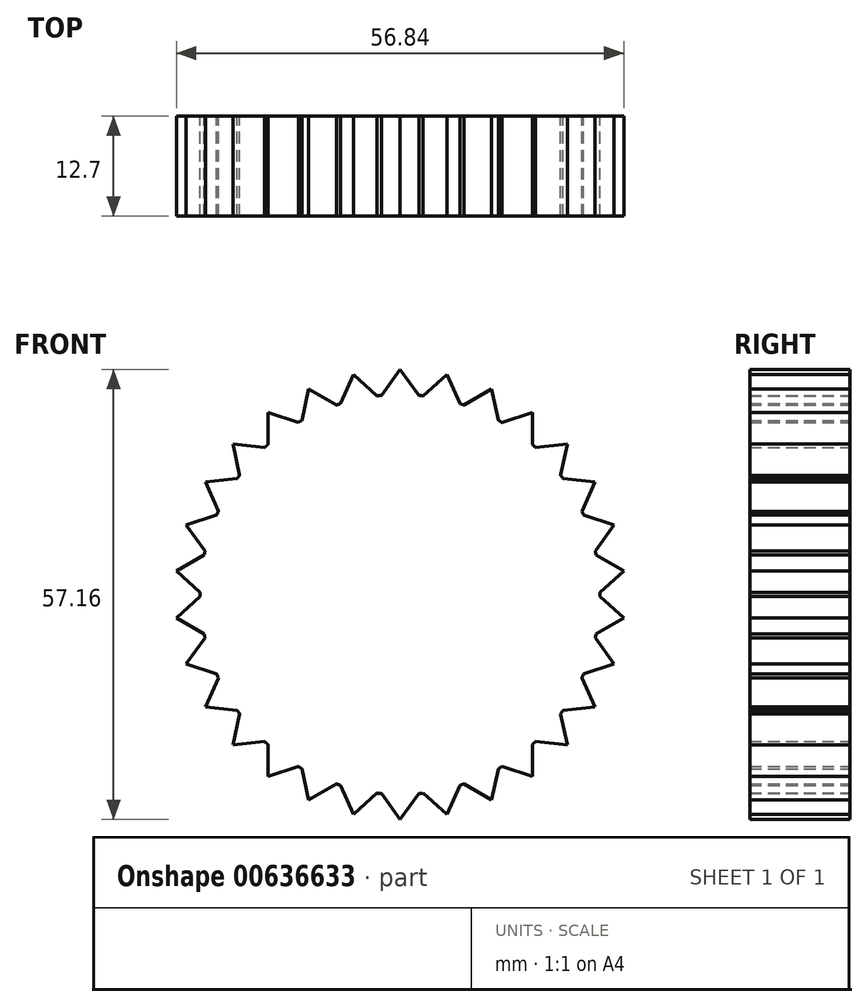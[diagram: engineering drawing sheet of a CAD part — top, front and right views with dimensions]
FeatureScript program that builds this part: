
annotation { "Feature Type Name" : "Feature", "Feature Type Description" : "" }
export const myFeature = defineFeature(function(context is Context, id is Id, definition is map)
    precondition{}
    {
        {
            var Q0;
            Q0=qCreatedBy(makeId("Front.planeOp"),FACE);
            var sketch = newSketch(context, id + "F0", { "sketchPlane" : qUnion([Q0])});
            skCircle(sketch, "E0", {"center": v(0, 0) * mm, "radius": 25.4 * mm});
            skLineSegment(sketch, "E1", {"start": v(0, 25.4) * mm, "end": v(0, 28.58) * mm});
            skLineSegment(sketch, "E2", {"start": v(0, 28.58) * mm, "end": v(-2.39, 25.29) * mm});
            skLineSegment(sketch, "E3.MirrorCS", {"start": v(0, 28.58) * mm, "end": v(2.39, 25.29) * mm});
            skLineSegment(sketch, "E4.1.0", {"start": v(-5.94, 27.95) * mm, "end": v(-7.6, 24.24) * mm});
            skLineSegment(sketch, "E4.1.1", {"start": v(-5.94, 27.95) * mm, "end": v(-2.92, 25.23) * mm});
            skLineSegment(sketch, "E4.2.0", {"start": v(-11.62, 26.1) * mm, "end": v(-12.47, 22.13) * mm});
            skLineSegment(sketch, "E4.2.1", {"start": v(-11.62, 26.1) * mm, "end": v(-8.1, 24.07) * mm});
            skLineSegment(sketch, "E4.3.0", {"start": v(-16.8, 23.12) * mm, "end": v(-16.8, 19.05) * mm});
            skLineSegment(sketch, "E4.3.1", {"start": v(-16.8, 23.12) * mm, "end": v(-12.93, 21.86) * mm});
            skLineSegment(sketch, "E4.4.0", {"start": v(-21.24, 19.12) * mm, "end": v(-20.4, 15.15) * mm});
            skLineSegment(sketch, "E4.4.1", {"start": v(-21.24, 19.12) * mm, "end": v(-17.2, 18.7) * mm});
            skLineSegment(sketch, "E4.5.0", {"start": v(-24.75, 14.29) * mm, "end": v(-23.1, 10.58) * mm});
            skLineSegment(sketch, "E4.5.1", {"start": v(-24.75, 14.29) * mm, "end": v(-20.7, 14.71) * mm});
            skLineSegment(sketch, "E4.6.0", {"start": v(-27.18, 8.83) * mm, "end": v(-24.79, 5.54) * mm});
            skLineSegment(sketch, "E4.6.1", {"start": v(-27.18, 8.83) * mm, "end": v(-23.31, 10.09) * mm});
            skLineSegment(sketch, "E4.7.0", {"start": v(-28.42, 2.99) * mm, "end": v(-25.4, 0.27) * mm});
            skLineSegment(sketch, "E4.7.1", {"start": v(-28.42, 2.99) * mm, "end": v(-24.9, 5.02) * mm});
            skLineSegment(sketch, "E4.8.0", {"start": v(-28.42, -2.99) * mm, "end": v(-24.9, -5.02) * mm});
            skLineSegment(sketch, "E4.8.1", {"start": v(-28.42, -2.99) * mm, "end": v(-25.4, -0.27) * mm});
            skLineSegment(sketch, "E4.9.0", {"start": v(-27.18, -8.83) * mm, "end": v(-23.31, -10.09) * mm});
            skLineSegment(sketch, "E4.9.1", {"start": v(-27.18, -8.83) * mm, "end": v(-24.79, -5.54) * mm});
            skLineSegment(sketch, "E4.10.0", {"start": v(-24.75, -14.29) * mm, "end": v(-20.7, -14.71) * mm});
            skLineSegment(sketch, "E4.10.1", {"start": v(-24.75, -14.29) * mm, "end": v(-23.1, -10.58) * mm});
            skLineSegment(sketch, "E4.11.0", {"start": v(-21.24, -19.12) * mm, "end": v(-17.2, -18.7) * mm});
            skLineSegment(sketch, "E4.11.1", {"start": v(-21.24, -19.12) * mm, "end": v(-20.4, -15.15) * mm});
            skLineSegment(sketch, "E4.12.0", {"start": v(-16.8, -23.12) * mm, "end": v(-12.93, -21.86) * mm});
            skLineSegment(sketch, "E4.12.1", {"start": v(-16.8, -23.12) * mm, "end": v(-16.8, -19.05) * mm});
            skLineSegment(sketch, "E4.13.0", {"start": v(-11.62, -26.1) * mm, "end": v(-8.1, -24.07) * mm});
            skLineSegment(sketch, "E4.13.1", {"start": v(-11.62, -26.1) * mm, "end": v(-12.47, -22.13) * mm});
            skLineSegment(sketch, "E4.14.0", {"start": v(-5.94, -27.95) * mm, "end": v(-2.92, -25.23) * mm});
            skLineSegment(sketch, "E4.14.1", {"start": v(-5.94, -27.95) * mm, "end": v(-7.6, -24.24) * mm});
            skLineSegment(sketch, "E4.15.0", {"start": v(0, -28.58) * mm, "end": v(2.39, -25.29) * mm});
            skLineSegment(sketch, "E4.15.1", {"start": v(0, -28.58) * mm, "end": v(-2.39, -25.29) * mm});
            skLineSegment(sketch, "E4.16.0", {"start": v(5.94, -27.95) * mm, "end": v(7.6, -24.24) * mm});
            skLineSegment(sketch, "E4.16.1", {"start": v(5.94, -27.95) * mm, "end": v(2.92, -25.23) * mm});
            skLineSegment(sketch, "E4.17.0", {"start": v(11.62, -26.1) * mm, "end": v(12.47, -22.13) * mm});
            skLineSegment(sketch, "E4.17.1", {"start": v(11.62, -26.1) * mm, "end": v(8.1, -24.07) * mm});
            skLineSegment(sketch, "E4.18.0", {"start": v(16.8, -23.12) * mm, "end": v(16.8, -19.05) * mm});
            skLineSegment(sketch, "E4.18.1", {"start": v(16.8, -23.12) * mm, "end": v(12.93, -21.86) * mm});
            skLineSegment(sketch, "E4.19.0", {"start": v(21.24, -19.12) * mm, "end": v(20.4, -15.15) * mm});
            skLineSegment(sketch, "E4.19.1", {"start": v(21.24, -19.12) * mm, "end": v(17.2, -18.7) * mm});
            skLineSegment(sketch, "E4.20.0", {"start": v(24.75, -14.29) * mm, "end": v(23.1, -10.58) * mm});
            skLineSegment(sketch, "E4.20.1", {"start": v(24.75, -14.29) * mm, "end": v(20.7, -14.71) * mm});
            skLineSegment(sketch, "E4.21.0", {"start": v(27.18, -8.83) * mm, "end": v(24.79, -5.54) * mm});
            skLineSegment(sketch, "E4.21.1", {"start": v(27.18, -8.83) * mm, "end": v(23.31, -10.09) * mm});
            skLineSegment(sketch, "E4.22.0", {"start": v(28.42, -2.99) * mm, "end": v(25.4, -0.27) * mm});
            skLineSegment(sketch, "E4.22.1", {"start": v(28.42, -2.99) * mm, "end": v(24.9, -5.02) * mm});
            skLineSegment(sketch, "E4.23.0", {"start": v(28.42, 2.99) * mm, "end": v(24.9, 5.02) * mm});
            skLineSegment(sketch, "E4.23.1", {"start": v(28.42, 2.99) * mm, "end": v(25.4, 0.27) * mm});
            skLineSegment(sketch, "E4.24.0", {"start": v(27.18, 8.83) * mm, "end": v(23.31, 10.09) * mm});
            skLineSegment(sketch, "E4.24.1", {"start": v(27.18, 8.83) * mm, "end": v(24.79, 5.54) * mm});
            skLineSegment(sketch, "E4.25.0", {"start": v(24.75, 14.29) * mm, "end": v(20.7, 14.71) * mm});
            skLineSegment(sketch, "E4.25.1", {"start": v(24.75, 14.29) * mm, "end": v(23.1, 10.58) * mm});
            skLineSegment(sketch, "E4.26.0", {"start": v(21.24, 19.12) * mm, "end": v(17.2, 18.7) * mm});
            skLineSegment(sketch, "E4.26.1", {"start": v(21.24, 19.12) * mm, "end": v(20.4, 15.15) * mm});
            skLineSegment(sketch, "E4.27.0", {"start": v(16.8, 23.12) * mm, "end": v(12.93, 21.86) * mm});
            skLineSegment(sketch, "E4.27.1", {"start": v(16.8, 23.12) * mm, "end": v(16.8, 19.05) * mm});
            skLineSegment(sketch, "E4.28.0", {"start": v(11.62, 26.1) * mm, "end": v(8.1, 24.07) * mm});
            skLineSegment(sketch, "E4.28.1", {"start": v(11.62, 26.1) * mm, "end": v(12.47, 22.13) * mm});
            skLineSegment(sketch, "E4.29.0", {"start": v(5.94, 27.95) * mm, "end": v(2.92, 25.23) * mm});
            skLineSegment(sketch, "E4.29.1", {"start": v(5.94, 27.95) * mm, "end": v(7.6, 24.24) * mm});
            skSolve(sketch);
        }
        {
            var Q0;
            {var subQ0=sQuery(id+"F0.wireOp",EDGE,"E0");var subQ33=makeQuery(id+"F0.imprint","INTERSECT",VERTEX,{"derivedFrom":[subQ0,sQuery(id+"F0.wireOp",EDGE,"E4.23.0")]});Q0=makeQuery(id+"F0.imprint","IMPRINT",FACE,{"disambiguationData":[TD([[makeQuery(id+"F0.imprint","IMPRINT",EDGE,{"disambiguationData":[TD([[subQ33,1.0]])],"derivedFrom":subQ0}),1.0]])]});}
            var Q1;
            {var subQ0=sQuery(id+"F0.wireOp",EDGE,"E4.26.0");Q1=makeQuery(id+"F0.imprint","IMPRINT",FACE,{"disambiguationData":[TD([[makeQuery(id+"F0.imprint","IMPRINT",EDGE,{"derivedFrom":subQ0}),1.0]])]});}
            var Q2;
            {var subQ0=sQuery(id+"F0.wireOp",EDGE,"E4.27.0");Q2=makeQuery(id+"F0.imprint","IMPRINT",FACE,{"disambiguationData":[TD([[makeQuery(id+"F0.imprint","IMPRINT",EDGE,{"derivedFrom":subQ0}),1.0]])]});}
            var Q3;
            {var subQ0=sQuery(id+"F0.wireOp",EDGE,"E4.28.0");Q3=makeQuery(id+"F0.imprint","IMPRINT",FACE,{"disambiguationData":[TD([[makeQuery(id+"F0.imprint","IMPRINT",EDGE,{"derivedFrom":subQ0}),1.0]])]});}
            var Q4;
            {var subQ0=sQuery(id+"F0.wireOp",EDGE,"E4.29.0");Q4=makeQuery(id+"F0.imprint","IMPRINT",FACE,{"disambiguationData":[TD([[makeQuery(id+"F0.imprint","IMPRINT",EDGE,{"derivedFrom":subQ0}),1.0]])]});}
            var Q5;
            {var subQ0=sQuery(id+"F0.wireOp",EDGE,"E1");Q5=makeQuery(id+"F0.imprint","IMPRINT",FACE,{"disambiguationData":[TD([[makeQuery(id+"F0.imprint","IMPRINT",EDGE,{"derivedFrom":subQ0}),-1.0]])]});}
            var Q6;
            {var subQ0=sQuery(id+"F0.wireOp",EDGE,"E4.25.0");Q6=makeQuery(id+"F0.imprint","IMPRINT",FACE,{"disambiguationData":[TD([[makeQuery(id+"F0.imprint","IMPRINT",EDGE,{"derivedFrom":subQ0}),1.0]])]});}
            var Q7;
            {var subQ0=sQuery(id+"F0.wireOp",EDGE,"E4.24.0");Q7=makeQuery(id+"F0.imprint","IMPRINT",FACE,{"disambiguationData":[TD([[makeQuery(id+"F0.imprint","IMPRINT",EDGE,{"derivedFrom":subQ0}),1.0]])]});}
            var Q8;
            {var subQ0=sQuery(id+"F0.wireOp",EDGE,"E4.23.0");Q8=makeQuery(id+"F0.imprint","IMPRINT",FACE,{"disambiguationData":[TD([[makeQuery(id+"F0.imprint","IMPRINT",EDGE,{"derivedFrom":subQ0}),1.0]])]});}
            var Q9;
            {var subQ0=sQuery(id+"F0.wireOp",EDGE,"E4.22.0");Q9=makeQuery(id+"F0.imprint","IMPRINT",FACE,{"disambiguationData":[TD([[makeQuery(id+"F0.imprint","IMPRINT",EDGE,{"derivedFrom":subQ0}),1.0]])]});}
            var Q10;
            {var subQ0=sQuery(id+"F0.wireOp",EDGE,"E4.21.0");Q10=makeQuery(id+"F0.imprint","IMPRINT",FACE,{"disambiguationData":[TD([[makeQuery(id+"F0.imprint","IMPRINT",EDGE,{"derivedFrom":subQ0}),1.0]])]});}
            var Q11;
            {var subQ0=sQuery(id+"F0.wireOp",EDGE,"E4.20.0");Q11=makeQuery(id+"F0.imprint","IMPRINT",FACE,{"disambiguationData":[TD([[makeQuery(id+"F0.imprint","IMPRINT",EDGE,{"derivedFrom":subQ0}),1.0]])]});}
            var Q12;
            {var subQ0=sQuery(id+"F0.wireOp",EDGE,"E4.19.0");Q12=makeQuery(id+"F0.imprint","IMPRINT",FACE,{"disambiguationData":[TD([[makeQuery(id+"F0.imprint","IMPRINT",EDGE,{"derivedFrom":subQ0}),1.0]])]});}
            var Q13;
            {var subQ0=sQuery(id+"F0.wireOp",EDGE,"E4.18.0");Q13=makeQuery(id+"F0.imprint","IMPRINT",FACE,{"disambiguationData":[TD([[makeQuery(id+"F0.imprint","IMPRINT",EDGE,{"derivedFrom":subQ0}),1.0]])]});}
            var Q14;
            {var subQ0=sQuery(id+"F0.wireOp",EDGE,"E4.17.0");Q14=makeQuery(id+"F0.imprint","IMPRINT",FACE,{"disambiguationData":[TD([[makeQuery(id+"F0.imprint","IMPRINT",EDGE,{"derivedFrom":subQ0}),1.0]])]});}
            var Q15;
            {var subQ0=sQuery(id+"F0.wireOp",EDGE,"E4.16.0");Q15=makeQuery(id+"F0.imprint","IMPRINT",FACE,{"disambiguationData":[TD([[makeQuery(id+"F0.imprint","IMPRINT",EDGE,{"derivedFrom":subQ0}),1.0]])]});}
            var Q16;
            {var subQ0=sQuery(id+"F0.wireOp",EDGE,"E4.15.0");Q16=makeQuery(id+"F0.imprint","IMPRINT",FACE,{"disambiguationData":[TD([[makeQuery(id+"F0.imprint","IMPRINT",EDGE,{"derivedFrom":subQ0}),1.0]])]});}
            var Q17;
            {var subQ0=sQuery(id+"F0.wireOp",EDGE,"E4.14.0");Q17=makeQuery(id+"F0.imprint","IMPRINT",FACE,{"disambiguationData":[TD([[makeQuery(id+"F0.imprint","IMPRINT",EDGE,{"derivedFrom":subQ0}),1.0]])]});}
            var Q18;
            {var subQ0=sQuery(id+"F0.wireOp",EDGE,"E4.13.0");Q18=makeQuery(id+"F0.imprint","IMPRINT",FACE,{"disambiguationData":[TD([[makeQuery(id+"F0.imprint","IMPRINT",EDGE,{"derivedFrom":subQ0}),1.0]])]});}
            var Q19;
            {var subQ0=sQuery(id+"F0.wireOp",EDGE,"E4.10.0");Q19=makeQuery(id+"F0.imprint","IMPRINT",FACE,{"disambiguationData":[TD([[makeQuery(id+"F0.imprint","IMPRINT",EDGE,{"derivedFrom":subQ0}),1.0]])]});}
            var Q20;
            {var subQ0=sQuery(id+"F0.wireOp",EDGE,"E4.9.0");Q20=makeQuery(id+"F0.imprint","IMPRINT",FACE,{"disambiguationData":[TD([[makeQuery(id+"F0.imprint","IMPRINT",EDGE,{"derivedFrom":subQ0}),1.0]])]});}
            var Q21;
            {var subQ0=sQuery(id+"F0.wireOp",EDGE,"E4.8.0");Q21=makeQuery(id+"F0.imprint","IMPRINT",FACE,{"disambiguationData":[TD([[makeQuery(id+"F0.imprint","IMPRINT",EDGE,{"derivedFrom":subQ0}),1.0]])]});}
            var Q22;
            {var subQ0=sQuery(id+"F0.wireOp",EDGE,"E4.7.0");Q22=makeQuery(id+"F0.imprint","IMPRINT",FACE,{"disambiguationData":[TD([[makeQuery(id+"F0.imprint","IMPRINT",EDGE,{"derivedFrom":subQ0}),1.0]])]});}
            var Q23;
            {var subQ0=sQuery(id+"F0.wireOp",EDGE,"E4.6.0");Q23=makeQuery(id+"F0.imprint","IMPRINT",FACE,{"disambiguationData":[TD([[makeQuery(id+"F0.imprint","IMPRINT",EDGE,{"derivedFrom":subQ0}),1.0]])]});}
            var Q24;
            {var subQ0=sQuery(id+"F0.wireOp",EDGE,"E4.5.0");Q24=makeQuery(id+"F0.imprint","IMPRINT",FACE,{"disambiguationData":[TD([[makeQuery(id+"F0.imprint","IMPRINT",EDGE,{"derivedFrom":subQ0}),1.0]])]});}
            var Q25;
            {var subQ0=sQuery(id+"F0.wireOp",EDGE,"E4.4.0");Q25=makeQuery(id+"F0.imprint","IMPRINT",FACE,{"disambiguationData":[TD([[makeQuery(id+"F0.imprint","IMPRINT",EDGE,{"derivedFrom":subQ0}),1.0]])]});}
            var Q26;
            {var subQ0=sQuery(id+"F0.wireOp",EDGE,"E4.3.0");Q26=makeQuery(id+"F0.imprint","IMPRINT",FACE,{"disambiguationData":[TD([[makeQuery(id+"F0.imprint","IMPRINT",EDGE,{"derivedFrom":subQ0}),1.0]])]});}
            var Q27;
            {var subQ0=sQuery(id+"F0.wireOp",EDGE,"E4.2.0");Q27=makeQuery(id+"F0.imprint","IMPRINT",FACE,{"disambiguationData":[TD([[makeQuery(id+"F0.imprint","IMPRINT",EDGE,{"derivedFrom":subQ0}),1.0]])]});}
            var Q28;
            {var subQ0=sQuery(id+"F0.wireOp",EDGE,"E4.1.0");Q28=makeQuery(id+"F0.imprint","IMPRINT",FACE,{"disambiguationData":[TD([[makeQuery(id+"F0.imprint","IMPRINT",EDGE,{"derivedFrom":subQ0}),1.0]])]});}
            var Q29;
            {var subQ0=sQuery(id+"F0.wireOp",EDGE,"E1");Q29=makeQuery(id+"F0.imprint","IMPRINT",FACE,{"disambiguationData":[TD([[makeQuery(id+"F0.imprint","IMPRINT",EDGE,{"derivedFrom":subQ0}),1.0]])]});}
            var Q30;
            {var subQ0=sQuery(id+"F0.wireOp",EDGE,"E4.12.0");Q30=makeQuery(id+"F0.imprint","IMPRINT",FACE,{"disambiguationData":[TD([[makeQuery(id+"F0.imprint","IMPRINT",EDGE,{"derivedFrom":subQ0}),1.0]])]});}
            var Q31;
            {var subQ0=sQuery(id+"F0.wireOp",EDGE,"E4.11.0");Q31=makeQuery(id+"F0.imprint","IMPRINT",FACE,{"disambiguationData":[TD([[makeQuery(id+"F0.imprint","IMPRINT",EDGE,{"derivedFrom":subQ0}),1.0]])]});}
            extrude(context, id + "F1", {"entities" : qUnion([Q0, Q1, Q2, Q3, Q4, Q5, Q6, Q7, Q8, Q9, Q10, Q11, Q12, Q13, Q14, Q15, Q16, Q17, Q18, Q19, Q20, Q21, Q22, Q23, Q24, Q25, Q26, Q27, Q28, Q29, Q30, Q31]), "depth" : 12.7 * mm, "offsetDistance" : 25.4 * mm});
        }
    });
